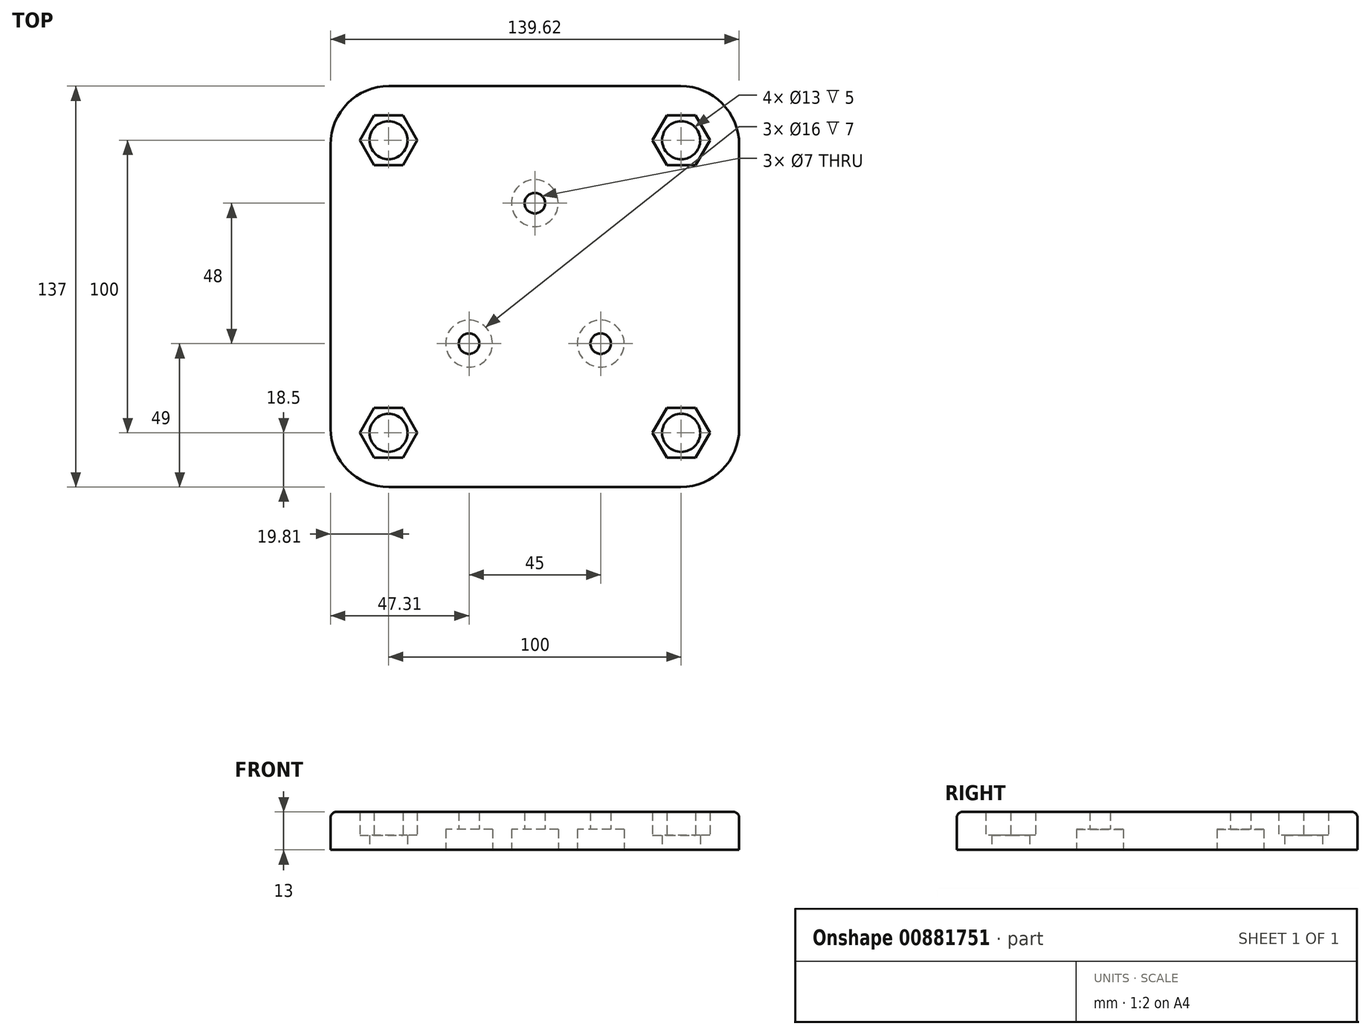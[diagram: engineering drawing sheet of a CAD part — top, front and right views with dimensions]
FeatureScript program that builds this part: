
annotation { "Feature Type Name" : "Feature", "Feature Type Description" : "" }
export const myFeature = defineFeature(function(context is Context, id is Id, definition is map)
    precondition{}
    {
        {
            var Q0;
            Q0=qCreatedBy(makeId("Top.planeOp"),FACE);
            var sketch = newSketch(context, id + "F0", { "sketchPlane" : qUnion([Q0])});
            skCircle(sketch, "E0.cCircle", {"center": v(0, 0) * mm, "radius": 8.5 * mm, "construction": true});
            skLineSegment(sketch, "E0.0", {"start": v(4.9, -8.5) * mm, "end": v(-4.9, -8.5) * mm});
            skLineSegment(sketch, "E0.1", {"start": v(-4.9, -8.5) * mm, "end": v(-9.81, 0) * mm});
            skLineSegment(sketch, "E0.2", {"start": v(-9.81, 0) * mm, "end": v(-4.9, 8.5) * mm});
            skLineSegment(sketch, "E0.3", {"start": v(-4.9, 8.5) * mm, "end": v(4.9, 8.5) * mm});
            skLineSegment(sketch, "E0.4", {"start": v(4.9, 8.5) * mm, "end": v(9.81, 0) * mm});
            skLineSegment(sketch, "E0.5", {"start": v(9.81, 0) * mm, "end": v(4.9, -8.5) * mm});
            skPoint(sketch, "E0.0.midPoint", {"position": v(0, -8.5) * mm});
            skCircle(sketch, "E1.cCircle", {"center": v(100, 0) * mm, "radius": 8.5 * mm, "construction": true});
            skLineSegment(sketch, "E1.0", {"start": v(104.9, -8.5) * mm, "end": v(95.1, -8.5) * mm});
            skLineSegment(sketch, "E1.1", {"start": v(95.1, -8.5) * mm, "end": v(90.19, 0) * mm});
            skLineSegment(sketch, "E1.2", {"start": v(90.19, 0) * mm, "end": v(95.1, 8.5) * mm});
            skLineSegment(sketch, "E1.3", {"start": v(95.1, 8.5) * mm, "end": v(104.9, 8.5) * mm});
            skLineSegment(sketch, "E1.4", {"start": v(104.9, 8.5) * mm, "end": v(109.81, 0) * mm});
            skLineSegment(sketch, "E1.5", {"start": v(109.81, 0) * mm, "end": v(104.9, -8.5) * mm});
            skPoint(sketch, "E1.0.midPoint", {"position": v(100, -8.5) * mm});
            skCircle(sketch, "E2.cCircle", {"center": v(0, -100) * mm, "radius": 8.5 * mm, "construction": true});
            skLineSegment(sketch, "E2.0", {"start": v(4.9, -108.5) * mm, "end": v(-4.9, -108.5) * mm});
            skLineSegment(sketch, "E2.1", {"start": v(-4.9, -108.5) * mm, "end": v(-9.81, -100) * mm});
            skLineSegment(sketch, "E2.2", {"start": v(-9.81, -100) * mm, "end": v(-4.9, -91.5) * mm});
            skLineSegment(sketch, "E2.3", {"start": v(-4.9, -91.5) * mm, "end": v(4.9, -91.5) * mm});
            skLineSegment(sketch, "E2.4", {"start": v(4.9, -91.5) * mm, "end": v(9.81, -100) * mm});
            skLineSegment(sketch, "E2.5", {"start": v(9.81, -100) * mm, "end": v(4.9, -108.5) * mm});
            skPoint(sketch, "E2.0.midPoint", {"position": v(0, -108.5) * mm});
            skCircle(sketch, "E3.cCircle", {"center": v(100, -100) * mm, "radius": 8.5 * mm, "construction": true});
            skLineSegment(sketch, "E3.0", {"start": v(104.9, -108.5) * mm, "end": v(95.1, -108.5) * mm});
            skLineSegment(sketch, "E3.1", {"start": v(95.1, -108.5) * mm, "end": v(90.19, -100) * mm});
            skLineSegment(sketch, "E3.2", {"start": v(90.19, -100) * mm, "end": v(95.1, -91.5) * mm});
            skLineSegment(sketch, "E3.3", {"start": v(95.1, -91.5) * mm, "end": v(104.9, -91.5) * mm});
            skLineSegment(sketch, "E3.4", {"start": v(104.9, -91.5) * mm, "end": v(109.81, -100) * mm});
            skLineSegment(sketch, "E3.5", {"start": v(109.81, -100) * mm, "end": v(104.9, -108.5) * mm});
            skPoint(sketch, "E3.0.midPoint", {"position": v(100, -108.5) * mm});
            skLineSegment(sketch, "E4", {"start": v(0, 0) * mm, "end": v(219.35, 0) * mm, "construction": true});
            skLineSegment(sketch, "E5", {"start": v(0, -100) * mm, "end": v(236.66, -100) * mm, "construction": true});
            skLineSegment(sketch, "E6", {"start": v(0, 0) * mm, "end": v(0, -167.8) * mm, "construction": true});
            skLineSegment(sketch, "E7.bottom", {"start": v(0.19, 18.5) * mm, "end": v(99.81, 18.5) * mm});
            skLineSegment(sketch, "E7.top", {"start": v(0.19, -118.5) * mm, "end": v(99.81, -118.5) * mm});
            skLineSegment(sketch, "E7.left", {"start": v(-19.81, -1.5) * mm, "end": v(-19.81, -98.5) * mm});
            skLineSegment(sketch, "E7.right", {"start": v(119.81, -1.5) * mm, "end": v(119.81, -98.5) * mm});
            skCircle(sketch, "E8", {"center": v(50, -21.5) * mm, "radius": 8 * mm});
            skCircle(sketch, "E9", {"center": v(50, -21.5) * mm, "radius": 3.5 * mm});
            skLineSegment(sketch, "E10", {"start": v(50, 18.5) * mm, "end": v(50, -118.5) * mm, "construction": true});
            skCircle(sketch, "E11", {"center": v(27.5, -69.5) * mm, "radius": 8 * mm});
            skCircle(sketch, "E12", {"center": v(27.5, -69.5) * mm, "radius": 3.5 * mm});
            skCircle(sketch, "E13", {"center": v(72.5, -69.5) * mm, "radius": 8 * mm});
            skCircle(sketch, "E14", {"center": v(72.5, -69.5) * mm, "radius": 3.5 * mm});
            skLineSegment(sketch, "E15", {"start": v(27.5, -66) * mm, "end": v(72.5, -66) * mm, "construction": true});
            skPoint(sketch, "E16.visualSharp", {"position": v(-19.81, -118.5) * mm});
            skArc(sketch, "E16.filletArc", {"start": v(-19.81, -98.5) * mm, "mid": v(-13.96, -112.64) * mm, "end": v(0.19, -118.5) * mm});
            skPoint(sketch, "E17.visualSharp", {"position": v(-19.81, 18.5) * mm});
            skArc(sketch, "E17.filletArc", {"start": v(0.19, 18.5) * mm, "mid": v(-13.96, 12.64) * mm, "end": v(-19.81, -1.5) * mm});
            skPoint(sketch, "E18.visualSharp", {"position": v(119.81, 18.5) * mm});
            skArc(sketch, "E18.filletArc", {"start": v(119.81, -1.5) * mm, "mid": v(113.96, 12.64) * mm, "end": v(99.81, 18.5) * mm});
            skPoint(sketch, "E19.visualSharp", {"position": v(119.81, -118.5) * mm});
            skArc(sketch, "E19.filletArc", {"start": v(99.81, -118.5) * mm, "mid": v(113.96, -112.64) * mm, "end": v(119.81, -98.5) * mm});
            skCircle(sketch, "E20", {"center": v(0, 0) * mm, "radius": 6.5 * mm});
            skCircle(sketch, "E21", {"center": v(100, 0) * mm, "radius": 6.5 * mm});
            skCircle(sketch, "E22", {"center": v(100, -100) * mm, "radius": 6.5 * mm});
            skCircle(sketch, "E23", {"center": v(0, -100) * mm, "radius": 6.5 * mm});
            skSolve(sketch);
        }
        {
            var Q0;
            Q0=qSketchRegion(id+"F0",true);
            var Q1;
            Q1=makeQuery(id+"F0.imprint","IMPRINT",FACE,{"disambiguationData":[TD([[makeQuery(id+"F0.imprint","IMPRINT",EDGE,{"derivedFrom":sQuery(id+"F0.wireOp",EDGE,"E0.0")}),-1.0]])]});
            var Q2;
            Q2=makeQuery(id+"F0.imprint","IMPRINT",FACE,{"disambiguationData":[TD([[makeQuery(id+"F0.imprint","IMPRINT",EDGE,{"derivedFrom":sQuery(id+"F0.wireOp",EDGE,"E8")}),1.0]])]});
            var Q3;
            Q3=makeQuery(id+"F0.imprint","IMPRINT",FACE,{"disambiguationData":[TD([[makeQuery(id+"F0.imprint","IMPRINT",EDGE,{"derivedFrom":sQuery(id+"F0.wireOp",EDGE,"E9")}),1.0]])]});
            var Q4;
            Q4=makeQuery(id+"F0.imprint","IMPRINT",FACE,{"disambiguationData":[TD([[makeQuery(id+"F0.imprint","IMPRINT",EDGE,{"derivedFrom":sQuery(id+"F0.wireOp",EDGE,"E1.0")}),-1.0]])]});
            var Q5;
            Q5=makeQuery(id+"F0.imprint","IMPRINT",FACE,{"disambiguationData":[TD([[makeQuery(id+"F0.imprint","IMPRINT",EDGE,{"derivedFrom":sQuery(id+"F0.wireOp",EDGE,"E13")}),1.0]])]});
            var Q6;
            Q6=makeQuery(id+"F0.imprint","IMPRINT",FACE,{"disambiguationData":[TD([[makeQuery(id+"F0.imprint","IMPRINT",EDGE,{"derivedFrom":sQuery(id+"F0.wireOp",EDGE,"E14")}),1.0]])]});
            var Q7;
            Q7=makeQuery(id+"F0.imprint","IMPRINT",FACE,{"disambiguationData":[TD([[makeQuery(id+"F0.imprint","IMPRINT",EDGE,{"derivedFrom":sQuery(id+"F0.wireOp",EDGE,"E11")}),1.0]])]});
            var Q8;
            Q8=makeQuery(id+"F0.imprint","IMPRINT",FACE,{"disambiguationData":[TD([[makeQuery(id+"F0.imprint","IMPRINT",EDGE,{"derivedFrom":sQuery(id+"F0.wireOp",EDGE,"E12")}),1.0]])]});
            var Q9;
            Q9=makeQuery(id+"F0.imprint","IMPRINT",FACE,{"disambiguationData":[TD([[makeQuery(id+"F0.imprint","IMPRINT",EDGE,{"derivedFrom":sQuery(id+"F0.wireOp",EDGE,"E2.0")}),-1.0]])]});
            var Q10;
            Q10=makeQuery(id+"F0.imprint","IMPRINT",FACE,{"disambiguationData":[TD([[makeQuery(id+"F0.imprint","IMPRINT",EDGE,{"derivedFrom":sQuery(id+"F0.wireOp",EDGE,"E3.0")}),-1.0]])]});
            extrude(context, id + "F1", {"entities" : qUnion([Q0, Q1, Q2, Q3, Q4, Q5, Q6, Q7, Q8, Q9, Q10]), "depth" : 13 * mm, "offsetDistance" : 25 * mm});
        }
        {
            var Q0;
            Q0=makeQuery(id+"F0.imprint","IMPRINT",FACE,{"disambiguationData":[TD([[makeQuery(id+"F0.imprint","IMPRINT",EDGE,{"derivedFrom":sQuery(id+"F0.wireOp",EDGE,"E0.0")}),-1.0]])]});
            var Q1;
            Q1=makeQuery(id+"F0.imprint","IMPRINT",FACE,{"disambiguationData":[TD([[makeQuery(id+"F0.imprint","IMPRINT",EDGE,{"derivedFrom":sQuery(id+"F0.wireOp",EDGE,"E3.0")}),-1.0]])]});
            var Q2;
            Q2=makeQuery(id+"F0.imprint","IMPRINT",FACE,{"disambiguationData":[TD([[makeQuery(id+"F0.imprint","IMPRINT",EDGE,{"derivedFrom":sQuery(id+"F0.wireOp",EDGE,"E2.0")}),-1.0]])]});
            var Q3;
            Q3=makeQuery(id+"F0.imprint","IMPRINT",FACE,{"disambiguationData":[TD([[makeQuery(id+"F0.imprint","IMPRINT",EDGE,{"derivedFrom":sQuery(id+"F0.wireOp",EDGE,"E1.0")}),-1.0]])]});
            var Q4;
            Q4=makeQuery(id+"F1.opExtrude","CAP_FACE",FACE,{"disambiguationData":[OSD([sQuery(id+"F0.wireOp",EDGE,"E7.bottom"),sQuery(id+"F0.wireOp",EDGE,"E7.top"),sQuery(id+"F0.wireOp",EDGE,"E7.left"),sQuery(id+"F0.wireOp",EDGE,"E7.right"),sQuery(id+"F0.wireOp",EDGE,"E16.filletArc"),sQuery(id+"F0.wireOp",EDGE,"E17.filletArc"),sQuery(id+"F0.wireOp",EDGE,"E18.filletArc"),sQuery(id+"F0.wireOp",EDGE,"E19.filletArc")])],"isStart":false});
            extrude(context, id + "F2", {"entities" : qUnion([Q0, Q1, Q2, Q3]), "operationType" : NewBodyOperationType.REMOVE, "endBound" : BoundingType.UP_TO_SURFACE, "depth" : 8 * mm, "endBoundEntityFace" : qUnion([Q4]), "offsetDistance" : 25 * mm});
        }
        {
            var Q0;
            Q0=makeQuery(id+"F0.imprint","IMPRINT",FACE,{"disambiguationData":[TD([[makeQuery(id+"F0.imprint","IMPRINT",EDGE,{"derivedFrom":sQuery(id+"F0.wireOp",EDGE,"E13")}),1.0]])]});
            var Q1;
            Q1=makeQuery(id+"F0.imprint","IMPRINT",FACE,{"disambiguationData":[TD([[makeQuery(id+"F0.imprint","IMPRINT",EDGE,{"derivedFrom":sQuery(id+"F0.wireOp",EDGE,"E11")}),1.0]])]});
            var Q2;
            Q2=makeQuery(id+"F0.imprint","IMPRINT",FACE,{"disambiguationData":[TD([[makeQuery(id+"F0.imprint","IMPRINT",EDGE,{"derivedFrom":sQuery(id+"F0.wireOp",EDGE,"E8")}),1.0]])]});
            extrude(context, id + "F3", {"entities" : qUnion([Q0, Q1, Q2]), "operationType" : NewBodyOperationType.REMOVE, "depth" : 7 * mm, "offsetDistance" : 25 * mm});
        }
        {
            var Q0;
            Q0=makeQuery(id+"F0.imprint","IMPRINT",FACE,{"disambiguationData":[TD([[makeQuery(id+"F0.imprint","IMPRINT",EDGE,{"derivedFrom":sQuery(id+"F0.wireOp",EDGE,"E12")}),1.0]])]});
            var Q1;
            Q1=makeQuery(id+"F0.imprint","IMPRINT",FACE,{"disambiguationData":[TD([[makeQuery(id+"F0.imprint","IMPRINT",EDGE,{"derivedFrom":sQuery(id+"F0.wireOp",EDGE,"E14")}),1.0]])]});
            var Q2;
            Q2=makeQuery(id+"F0.imprint","IMPRINT",FACE,{"disambiguationData":[TD([[makeQuery(id+"F0.imprint","IMPRINT",EDGE,{"derivedFrom":sQuery(id+"F0.wireOp",EDGE,"E9")}),1.0]])]});
            var Q3;
            Q3=makeQuery(id+"F1.opExtrude","CAP_FACE",FACE,{"disambiguationData":[OSD([sQuery(id+"F0.wireOp",EDGE,"E7.bottom"),sQuery(id+"F0.wireOp",EDGE,"E7.top"),sQuery(id+"F0.wireOp",EDGE,"E7.left"),sQuery(id+"F0.wireOp",EDGE,"E7.right")])],"isStart":false});
            extrude(context, id + "F4", {"entities" : qUnion([Q0, Q1, Q2]), "operationType" : NewBodyOperationType.REMOVE, "endBound" : BoundingType.UP_TO_SURFACE, "depth" : 25 * mm, "endBoundEntityFace" : qUnion([Q3]), "offsetDistance" : 25 * mm});
        }
        {
            var Q0;
            Q0=makeQuery(id+"F0.imprint","IMPRINT",FACE,{"disambiguationData":[TD([[makeQuery(id+"F0.imprint","IMPRINT",EDGE,{"derivedFrom":sQuery(id+"F0.wireOp",EDGE,"E0.0")}),-1.0]])]});
            var Q1;
            Q1=makeQuery(id+"F0.imprint","IMPRINT",FACE,{"disambiguationData":[TD([[makeQuery(id+"F0.imprint","IMPRINT",EDGE,{"derivedFrom":sQuery(id+"F0.wireOp",EDGE,"E1.0")}),-1.0]])]});
            var Q2;
            Q2=makeQuery(id+"F0.imprint","IMPRINT",FACE,{"disambiguationData":[TD([[makeQuery(id+"F0.imprint","IMPRINT",EDGE,{"derivedFrom":sQuery(id+"F0.wireOp",EDGE,"E3.0")}),-1.0]])]});
            var Q3;
            Q3=makeQuery(id+"F0.imprint","IMPRINT",FACE,{"disambiguationData":[TD([[makeQuery(id+"F0.imprint","IMPRINT",EDGE,{"derivedFrom":sQuery(id+"F0.wireOp",EDGE,"E2.0")}),-1.0]])]});
            extrude(context, id + "F5", {"entities" : qUnion([Q0, Q1, Q2, Q3]), "operationType" : NewBodyOperationType.ADD, "depth" : 5 * mm, "offsetDistance" : 25 * mm});
        }
        {
            var Q0;
            Q0=makeQuery(id+"F0.imprint","IMPRINT",FACE,{"disambiguationData":[TD([[makeQuery(id+"F0.imprint","IMPRINT",EDGE,{"derivedFrom":sQuery(id+"F0.wireOp",EDGE,"E20")}),1.0]])]});
            var Q1;
            Q1=makeQuery(id+"F0.imprint","IMPRINT",FACE,{"disambiguationData":[TD([[makeQuery(id+"F0.imprint","IMPRINT",EDGE,{"derivedFrom":sQuery(id+"F0.wireOp",EDGE,"E21")}),1.0]])]});
            var Q2;
            Q2=makeQuery(id+"F0.imprint","IMPRINT",FACE,{"disambiguationData":[TD([[makeQuery(id+"F0.imprint","IMPRINT",EDGE,{"derivedFrom":sQuery(id+"F0.wireOp",EDGE,"E22")}),1.0]])]});
            var Q3;
            Q3=makeQuery(id+"F0.imprint","IMPRINT",FACE,{"disambiguationData":[TD([[makeQuery(id+"F0.imprint","IMPRINT",EDGE,{"derivedFrom":sQuery(id+"F0.wireOp",EDGE,"E23")}),1.0]])]});
            var Q4;
            Q4=makeQuery(id+"F5.opExtrude","CAP_FACE",FACE,{"disambiguationData":[OSD([sQuery(id+"F0.wireOp",EDGE,"E0.0"),sQuery(id+"F0.wireOp",EDGE,"E0.1"),sQuery(id+"F0.wireOp",EDGE,"E0.2"),sQuery(id+"F0.wireOp",EDGE,"E0.3"),sQuery(id+"F0.wireOp",EDGE,"E0.4"),sQuery(id+"F0.wireOp",EDGE,"E0.5"),sQuery(id+"F0.wireOp",EDGE,"E20")])],"isStart":false});
            extrude(context, id + "F6", {"entities" : qUnion([Q0, Q1, Q2, Q3]), "operationType" : NewBodyOperationType.REMOVE, "endBound" : BoundingType.UP_TO_SURFACE, "depth" : 5 * mm, "endBoundEntityFace" : qUnion([Q4]), "offsetDistance" : 25 * mm});
        }
        {
            var Q0;
            Q0=makeQuery(id+"F1.opExtrude","CAP_EDGE",EDGE,{"disambiguationData":[OSD([sQuery(id+"F0.wireOp",EDGE,"E7.right")])],"isStart":false});
            fillet(context, id + "F7", {"entities" : qUnion([Q0]), "radius" : 2 * mm, "tangentPropagation" : true, "allowEdgeOverflow" : false});
        }
    });
